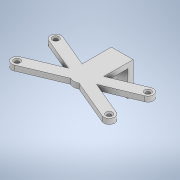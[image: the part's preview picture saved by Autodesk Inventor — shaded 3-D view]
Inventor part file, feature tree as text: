
AUTODESK INVENTOR PART (.ipt)
format: ipt  version: 2021 (Build 250183000, 183)  size: 205,312 bytes
history: native  units: mm
features: extrude x4, sketch x2, other x1, plane x1, chamfer x1
ambient origin geometry x8: Origin, YZ Plane, XZ Plane, XY Plane, X Axis, Y Axis, Z Axis, Center Point
bodies: Body1 (feature_tree)
feature tree (9):
  other  "HC-SR04.ipt"
  extrude  "Extrusion1"  Depth=10.0mm
  extrude  "Extrusion2"  Depth=5.0mm
  plane  "Arbeitsebene1"
  extrude  "Extrusion3"  Depth=5.0mm
  extrude  "Extrusion4"  Depth=5.0mm
  chamfer  "Fase1"  Distance=5.0mm
  sketch  "Skizze3"  dims[d0=10.0mm d1=1.8mm]
  sketch  "Skizze4"  dims[d3=8.0mm d5=5.0mm d6=5.0mm d7=5.0mm d8=5.0mm d9=5.0mm d10=5.0mm d11=5.0mm d12=5.0mm d13=3.0mm d14=10.0mm d15=8.0mm d16=2.4mm d17=2.4mm d18=0.0mm d19=12.0mm d20=0.0mm d21=2.4mm d22=0.0mm d23=0.0mm d25=15.620499mm d26=1.859583mm d27=4.506833mm d28=4.2mm d30=4.506833mm d31=12.0mm d32=0.0mm d33=0.6mm d34=2.0mm d35=45.0deg]
